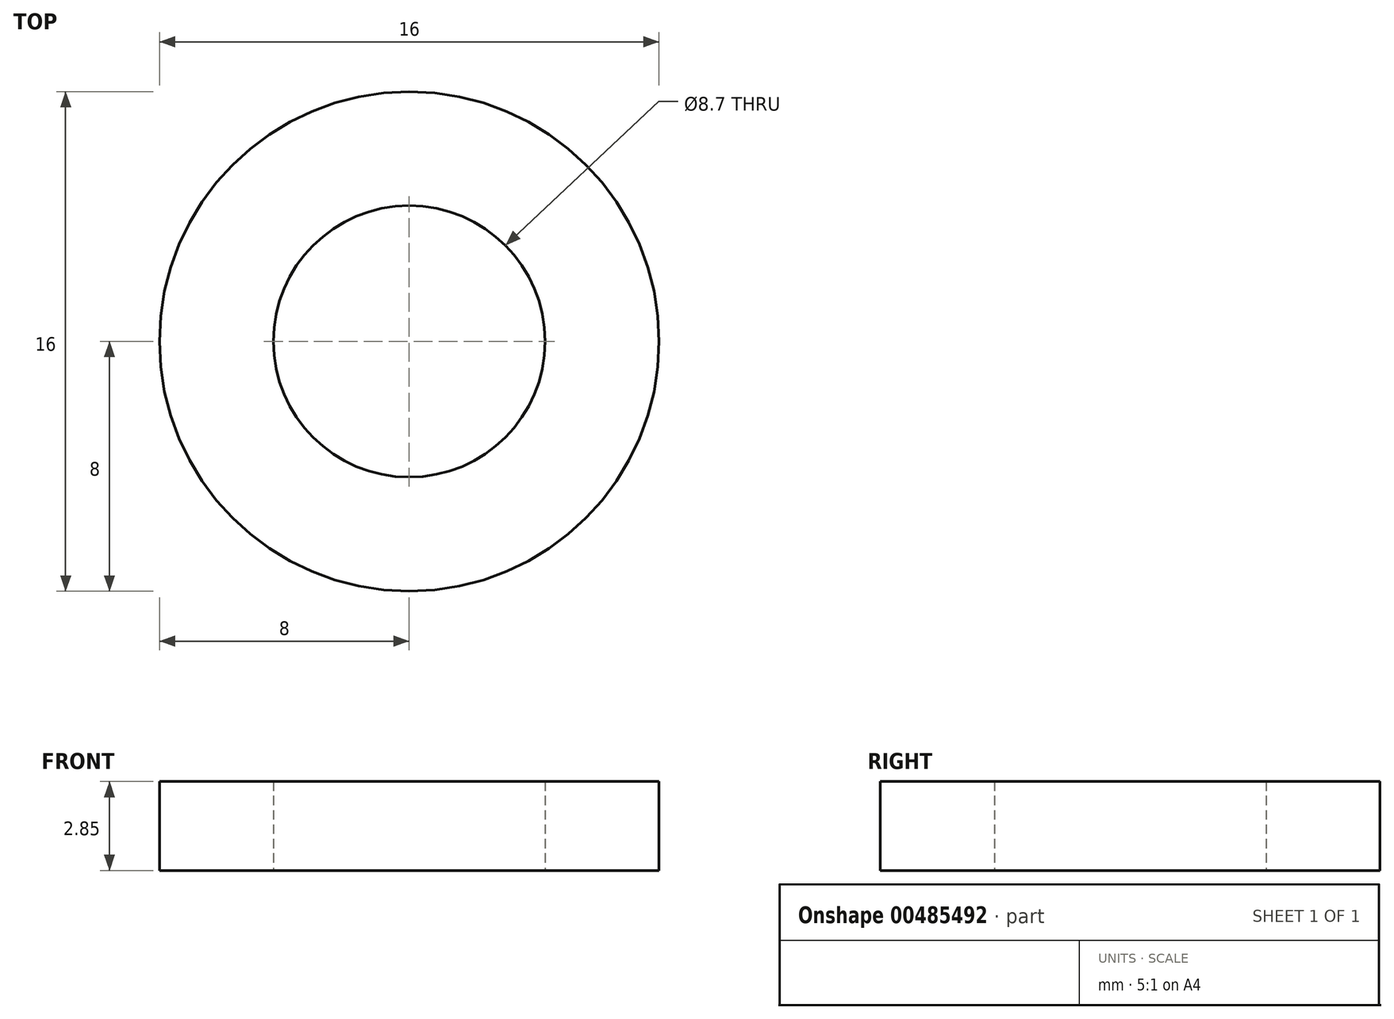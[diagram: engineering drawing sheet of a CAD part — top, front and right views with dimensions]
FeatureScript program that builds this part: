
annotation { "Feature Type Name" : "Feature", "Feature Type Description" : "" }
export const myFeature = defineFeature(function(context is Context, id is Id, definition is map)
    precondition{}
    {
        {
            var Q0;
            Q0=qCreatedBy(makeId("Top.planeOp"),FACE);
            var sketch = newSketch(context, id + "F0", { "sketchPlane" : qUnion([Q0])});
            skCircle(sketch, "E0", {"center": v(0, 0) * mm, "radius": 4.15 * mm, "construction": true});
            skCircle(sketch, "E1", {"center": v(0, 0) * mm, "radius": 8 * mm});
            skCircle(sketch, "E2.0", {"center": v(0, 0) * mm, "radius": 4.35 * mm});
            skSolve(sketch);
        }
        {
            var Q0;
            Q0 = qSketchRegion(id + "F0", true);
            extrude(context, id + "F1", {"entities" : qUnion([Q0]), "depth" : 2.85 * mm});
        }
    });
